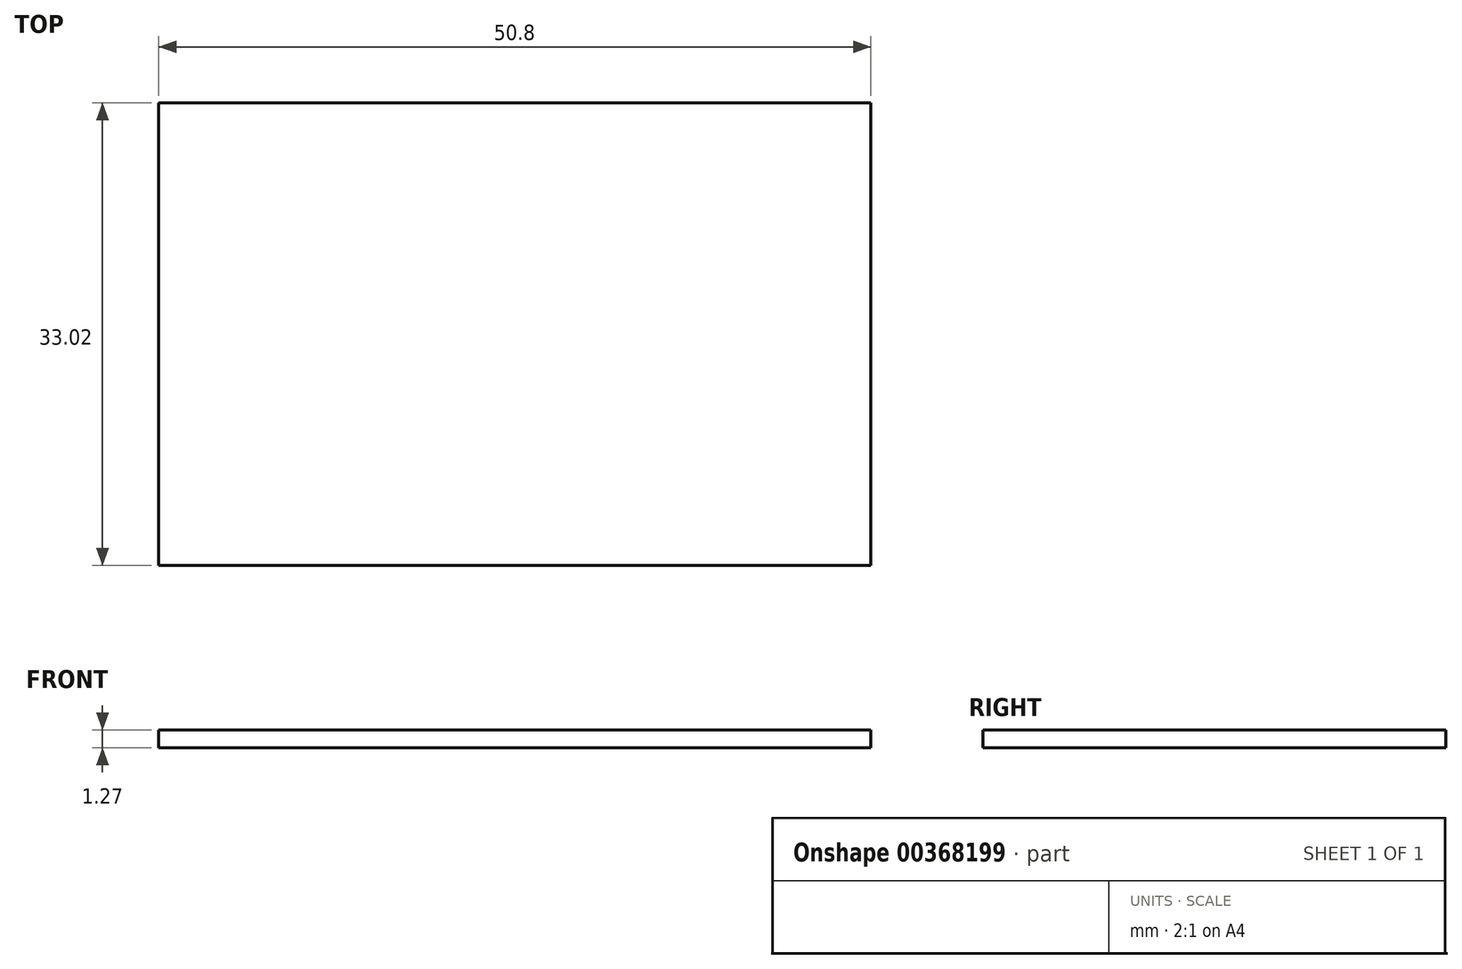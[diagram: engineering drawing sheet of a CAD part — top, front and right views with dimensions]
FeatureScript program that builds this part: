
annotation { "Feature Type Name" : "Feature", "Feature Type Description" : "" }
export const myFeature = defineFeature(function(context is Context, id is Id, definition is map)
    precondition{}
    {
        {
            var Q0;
            Q0=qCreatedBy(makeId("Top.planeOp"),FACE);
            var sketch = newSketch(context, id + "F0", { "sketchPlane" : qUnion([Q0])});
            skLineSegment(sketch, "E0.bottom", {"start": v(0, 0) * mm, "end": v(50.8, 0) * mm});
            skLineSegment(sketch, "E0.top", {"start": v(0, 33.02) * mm, "end": v(50.8, 33.02) * mm});
            skLineSegment(sketch, "E0.left", {"start": v(0, 0) * mm, "end": v(0, 33.02) * mm});
            skLineSegment(sketch, "E0.right", {"start": v(50.8, 0) * mm, "end": v(50.8, 33.02) * mm});
            skSolve(sketch);
        }
        {
            var Q0;
            Q0 = qSketchRegion(id + "F0", true);
            extrude(context, id + "F1", {"entities" : qUnion([Q0]), "depth" : 1.27 * mm, "offsetDistance" : 25.4 * mm});
        }
    });
